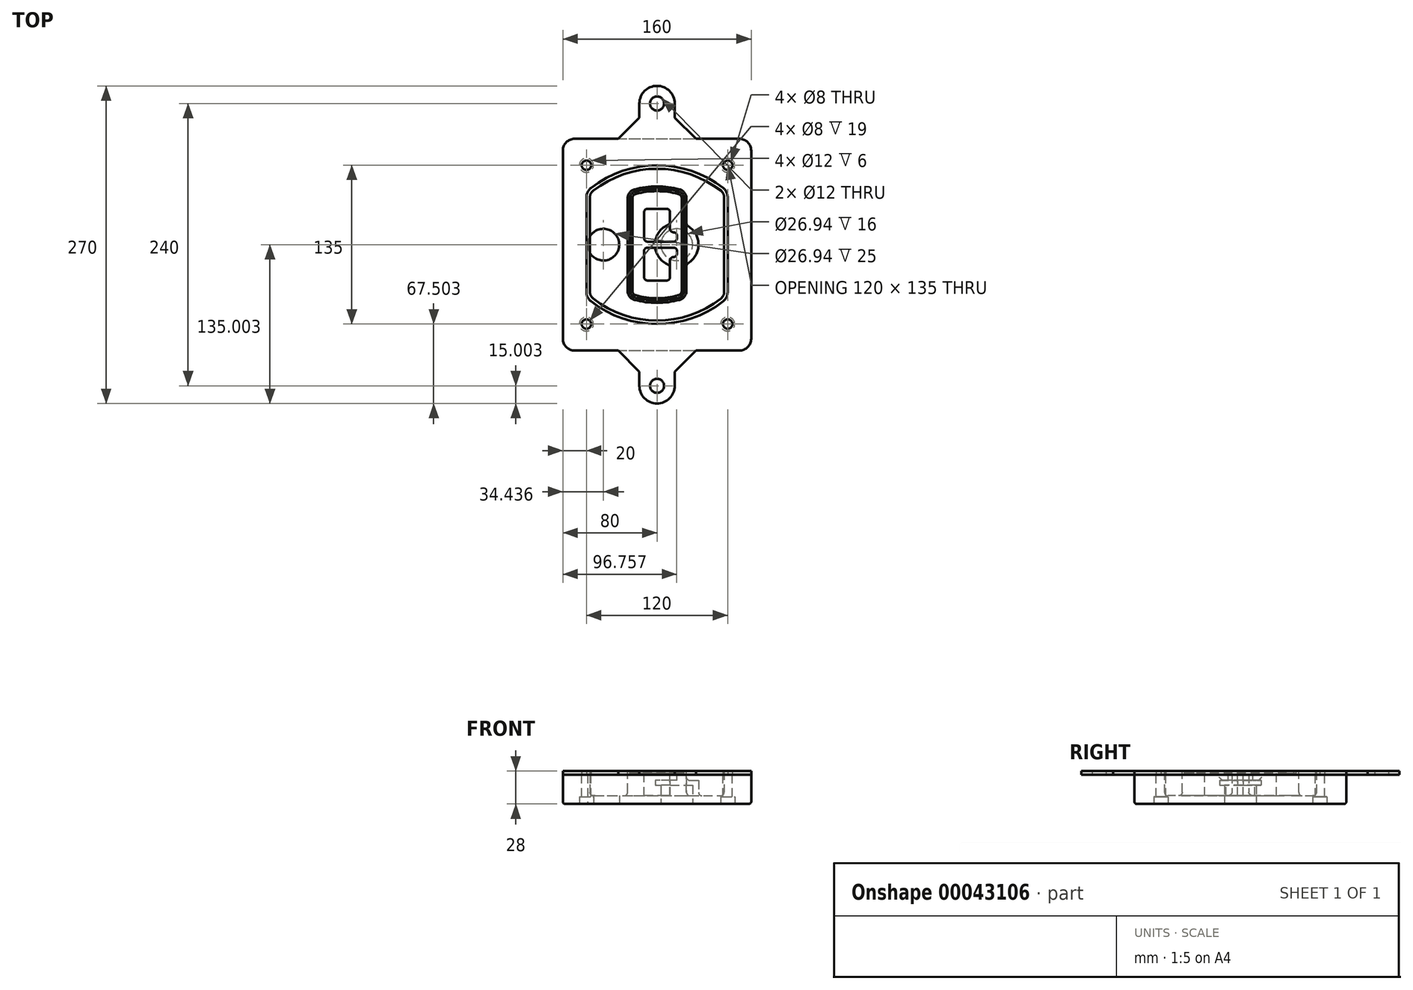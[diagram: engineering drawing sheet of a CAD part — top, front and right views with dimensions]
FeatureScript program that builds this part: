
annotation { "Feature Type Name" : "Feature", "Feature Type Description" : "" }
export const myFeature = defineFeature(function(context is Context, id is Id, definition is map)
    precondition{}
    {
        {
            var Q0;
            Q0=qCreatedBy(makeId("Top.planeOp"),FACE);
            var sketch = newSketch(context, id + "F0", { "sketchPlane" : qUnion([Q0])});
            skPoint(sketch, "E0.rect.middle", {"position": v(0, 0) * mm});
            skLineSegment(sketch, "E1.bottom", {"start": v(24.05, 28.38) * mm, "end": v(164.05, 28.38) * mm});
            skLineSegment(sketch, "E1.top", {"start": v(24.05, 208.38) * mm, "end": v(164.05, 208.38) * mm});
            skLineSegment(sketch, "E1.left", {"start": v(14.05, 38.38) * mm, "end": v(14.05, 198.38) * mm});
            skLineSegment(sketch, "E1.right", {"start": v(174.05, 38.38) * mm, "end": v(174.05, 198.38) * mm});
            skLineSegment(sketch, "E2", {"start": v(14.05, 208.38) * mm, "end": v(174.05, 28.38) * mm, "construction": true});
            skLineSegment(sketch, "E3", {"start": v(174.05, 208.38) * mm, "end": v(14.05, 28.38) * mm, "construction": true});
            skCircle(sketch, "E4", {"center": v(34.05, 185.88) * mm, "radius": 4 * mm});
            skCircle(sketch, "E5", {"center": v(154.05, 185.88) * mm, "radius": 4 * mm});
            skCircle(sketch, "E6", {"center": v(154.05, 50.88) * mm, "radius": 4 * mm});
            skCircle(sketch, "E7", {"center": v(34.05, 50.88) * mm, "radius": 4 * mm});
            skLineSegment(sketch, "E8", {"start": v(34.05, 185.88) * mm, "end": v(154.05, 185.88) * mm, "construction": true});
            skLineSegment(sketch, "E9", {"start": v(154.05, 185.88) * mm, "end": v(154.05, 50.88) * mm, "construction": true});
            skLineSegment(sketch, "E10", {"start": v(154.05, 50.88) * mm, "end": v(34.05, 50.88) * mm, "construction": true});
            skLineSegment(sketch, "E11", {"start": v(34.05, 50.88) * mm, "end": v(34.05, 185.88) * mm, "construction": true});
            skLineSegment(sketch, "E12", {"start": v(34.05, 158.68) * mm, "end": v(34.05, 78.09) * mm});
            skLineSegment(sketch, "E13", {"start": v(154.05, 158.68) * mm, "end": v(154.05, 78.09) * mm});
            skArc(sketch, "E14", {"start": v(150.2, 166.56) * mm, "mid": v(94.05, 185.88) * mm, "end": v(37.9, 166.56) * mm});
            skArc(sketch, "E15", {"start": v(37.9, 70.2) * mm, "mid": v(94.05, 50.88) * mm, "end": v(150.2, 70.2) * mm});
            skLineSegment(sketch, "E16", {"start": v(34.05, 118.38) * mm, "end": v(154.05, 118.38) * mm, "construction": true});
            skPoint(sketch, "E17.visualSharp", {"position": v(34.05, 73.38) * mm});
            skArc(sketch, "E17.filletArc", {"start": v(34.05, 78.09) * mm, "mid": v(35.06, 73.7) * mm, "end": v(37.9, 70.2) * mm});
            skPoint(sketch, "E18.visualSharp", {"position": v(34.05, 163.38) * mm});
            skArc(sketch, "E18.filletArc", {"start": v(37.9, 166.56) * mm, "mid": v(35.06, 163.06) * mm, "end": v(34.05, 158.68) * mm});
            skPoint(sketch, "E19.visualSharp", {"position": v(154.05, 163.38) * mm});
            skArc(sketch, "E19.filletArc", {"start": v(154.05, 158.68) * mm, "mid": v(153.04, 163.06) * mm, "end": v(150.2, 166.56) * mm});
            skPoint(sketch, "E20.visualSharp", {"position": v(154.05, 73.38) * mm});
            skArc(sketch, "E20.filletArc", {"start": v(150.2, 70.2) * mm, "mid": v(153.04, 73.7) * mm, "end": v(154.05, 78.09) * mm});
            skPoint(sketch, "E21.visualSharp", {"position": v(14.05, 208.38) * mm});
            skArc(sketch, "E21.filletArc", {"start": v(24.05, 208.38) * mm, "mid": v(16.98, 205.45) * mm, "end": v(14.05, 198.38) * mm});
            skPoint(sketch, "E22.visualSharp", {"position": v(174.05, 208.38) * mm});
            skArc(sketch, "E22.filletArc", {"start": v(174.05, 198.38) * mm, "mid": v(171.12, 205.45) * mm, "end": v(164.05, 208.38) * mm});
            skPoint(sketch, "E23.visualSharp", {"position": v(174.05, 28.38) * mm});
            skArc(sketch, "E23.filletArc", {"start": v(164.05, 28.38) * mm, "mid": v(171.12, 31.31) * mm, "end": v(174.05, 38.38) * mm});
            skPoint(sketch, "E24.visualSharp", {"position": v(14.05, 28.38) * mm});
            skArc(sketch, "E24.filletArc", {"start": v(14.05, 38.38) * mm, "mid": v(16.98, 31.31) * mm, "end": v(24.05, 28.38) * mm});
            skArc(sketch, "E25.0", {"start": v(151.05, 158.68) * mm, "mid": v(150.34, 161.75) * mm, "end": v(148.36, 164.2) * mm});
            skLineSegment(sketch, "E25.1", {"start": v(151.05, 158.68) * mm, "end": v(151.05, 78.09) * mm});
            skArc(sketch, "E25.2", {"start": v(148.36, 72.57) * mm, "mid": v(150.34, 75.02) * mm, "end": v(151.05, 78.09) * mm});
            skArc(sketch, "E25.3", {"start": v(39.74, 72.57) * mm, "mid": v(94.05, 53.88) * mm, "end": v(148.36, 72.57) * mm});
            skArc(sketch, "E25.4", {"start": v(37.05, 78.09) * mm, "mid": v(37.76, 75.02) * mm, "end": v(39.74, 72.57) * mm});
            skArc(sketch, "E25.5", {"start": v(148.36, 164.2) * mm, "mid": v(94.05, 182.88) * mm, "end": v(39.74, 164.2) * mm});
            skLineSegment(sketch, "E25.6", {"start": v(37.05, 158.68) * mm, "end": v(37.05, 78.09) * mm});
            skArc(sketch, "E25.7", {"start": v(39.74, 164.2) * mm, "mid": v(37.76, 161.75) * mm, "end": v(37.05, 158.68) * mm});
            skArc(sketch, "E26.0", {"start": v(35.43, 169.71) * mm, "mid": v(31.47, 164.82) * mm, "end": v(30.05, 158.68) * mm});
            skArc(sketch, "E26.1", {"start": v(152.67, 169.71) * mm, "mid": v(94.05, 189.88) * mm, "end": v(35.43, 169.71) * mm});
            skArc(sketch, "E26.2", {"start": v(158.05, 158.68) * mm, "mid": v(156.63, 164.82) * mm, "end": v(152.67, 169.71) * mm});
            skLineSegment(sketch, "E26.3", {"start": v(158.05, 158.68) * mm, "end": v(158.05, 78.09) * mm});
            skArc(sketch, "E26.4", {"start": v(152.67, 67.05) * mm, "mid": v(156.63, 71.95) * mm, "end": v(158.05, 78.09) * mm});
            skLineSegment(sketch, "E26.5", {"start": v(30.05, 158.68) * mm, "end": v(30.05, 78.09) * mm});
            skArc(sketch, "E26.6", {"start": v(35.43, 67.05) * mm, "mid": v(94.05, 46.88) * mm, "end": v(152.67, 67.05) * mm});
            skArc(sketch, "E26.7", {"start": v(30.05, 78.09) * mm, "mid": v(31.47, 71.95) * mm, "end": v(35.43, 67.05) * mm});
            skSolve(sketch);
        }
        {
            var Q0;
            Q0=makeQuery(id+"F0.imprint","IMPRINT",FACE,{"disambiguationData":[TD([[makeQuery(id+"F0.imprint","IMPRINT",EDGE,{"derivedFrom":sQuery(id+"F0.wireOp",EDGE,"E1.bottom")}),1.0]])]});
            var Q1;
            Q1=makeQuery(id+"F0.imprint","IMPRINT",FACE,{"disambiguationData":[TD([[makeQuery(id+"F0.imprint","IMPRINT",EDGE,{"derivedFrom":sQuery(id+"F0.wireOp",EDGE,"E12")}),1.0]])]});
            var Q2;
            Q2=makeQuery(id+"F0.imprint","IMPRINT",FACE,{"disambiguationData":[TD([[makeQuery(id+"F0.imprint","IMPRINT",EDGE,{"derivedFrom":sQuery(id+"F0.wireOp",EDGE,"E25.0")}),1.0]])]});
            var Q3;
            Q3=makeQuery(id+"F0.imprint","IMPRINT",FACE,{"disambiguationData":[TD([[makeQuery(id+"F0.imprint","IMPRINT",EDGE,{"derivedFrom":sQuery(id+"F0.wireOp",EDGE,"E12")}),-1.0]])]});
            extrude(context, id + "F1", {"entities" : qUnion([Q0, Q1, Q2, Q3]), "oppositeDirection" : true, "depth" : 25 * mm});
        }
        {
            var Q0;
            Q0=makeQuery(id+"F0.imprint","IMPRINT",FACE,{"disambiguationData":[TD([[makeQuery(id+"F0.imprint","IMPRINT",EDGE,{"derivedFrom":sQuery(id+"F0.wireOp",EDGE,"E12")}),1.0]])]});
            extrude(context, id + "F2", {"entities" : qUnion([Q0]), "operationType" : NewBodyOperationType.ADD, "depth" : 3 * mm});
        }
        {
            var Q0;
            Q0=makeQuery(id+"F0.imprint","IMPRINT",FACE,{"disambiguationData":[TD([[makeQuery(id+"F0.imprint","IMPRINT",EDGE,{"derivedFrom":sQuery(id+"F0.wireOp",EDGE,"E25.0")}),1.0]])]});
            extrude(context, id + "F3", {"entities" : qUnion([Q0]), "operationType" : NewBodyOperationType.REMOVE, "oppositeDirection" : true, "depth" : 18 * mm});
        }
        {
            var Q0;
            Q0=makeQuery(id+"F2.opExtrude","CAP_FACE",FACE,{"disambiguationData":[OSD([sQuery(id+"F0.wireOp",EDGE,"E12"),sQuery(id+"F0.wireOp",EDGE,"E13"),sQuery(id+"F0.wireOp",EDGE,"E14"),sQuery(id+"F0.wireOp",EDGE,"E15"),sQuery(id+"F0.wireOp",EDGE,"E17.filletArc"),sQuery(id+"F0.wireOp",EDGE,"E18.filletArc"),sQuery(id+"F0.wireOp",EDGE,"E19.filletArc"),sQuery(id+"F0.wireOp",EDGE,"E20.filletArc"),sQuery(id+"F0.wireOp",EDGE,"E25.0"),sQuery(id+"F0.wireOp",EDGE,"E25.1"),sQuery(id+"F0.wireOp",EDGE,"E25.2"),sQuery(id+"F0.wireOp",EDGE,"E25.3"),sQuery(id+"F0.wireOp",EDGE,"E25.4"),sQuery(id+"F0.wireOp",EDGE,"E25.5"),sQuery(id+"F0.wireOp",EDGE,"E25.6"),sQuery(id+"F0.wireOp",EDGE,"E25.7")])],"isStart":false});
            var sketch = newSketch(context, id + "F4", { "sketchPlane" : qUnion([Q0])});
            skArc(sketch, "E27.0", {"start": v(74.97, 71.41) * mm, "mid": v(94.05, 68.88) * mm, "end": v(113.13, 71.41) * mm});
            skArc(sketch, "E28.0", {"start": v(113.13, 165.35) * mm, "mid": v(94.05, 167.88) * mm, "end": v(74.97, 165.35) * mm});
            skLineSegment(sketch, "E29", {"start": v(69.05, 157.63) * mm, "end": v(69.05, 79.14) * mm});
            skLineSegment(sketch, "E30", {"start": v(119.05, 157.63) * mm, "end": v(119.05, 79.14) * mm});
            skLineSegment(sketch, "E31", {"start": v(69.05, 163.48) * mm, "end": v(119.05, 163.48) * mm, "construction": true});
            skLineSegment(sketch, "E32", {"start": v(69.05, 73.28) * mm, "end": v(119.05, 73.28) * mm, "construction": true});
            skPoint(sketch, "E33.visualSharp", {"position": v(69.05, 163.48) * mm});
            skArc(sketch, "E33.filletArc", {"start": v(74.97, 165.35) * mm, "mid": v(70.7, 162.5) * mm, "end": v(69.05, 157.63) * mm});
            skPoint(sketch, "E34.visualSharp", {"position": v(119.05, 163.48) * mm});
            skArc(sketch, "E34.filletArc", {"start": v(119.05, 157.63) * mm, "mid": v(117.4, 162.5) * mm, "end": v(113.13, 165.35) * mm});
            skPoint(sketch, "E35.visualSharp", {"position": v(119.05, 73.28) * mm});
            skArc(sketch, "E35.filletArc", {"start": v(113.13, 71.41) * mm, "mid": v(117.4, 74.27) * mm, "end": v(119.05, 79.14) * mm});
            skPoint(sketch, "E36.visualSharp", {"position": v(69.05, 73.28) * mm});
            skArc(sketch, "E36.filletArc", {"start": v(69.05, 79.14) * mm, "mid": v(70.7, 74.27) * mm, "end": v(74.97, 71.41) * mm});
            skArc(sketch, "E37.0", {"start": v(148.36, 164.2) * mm, "mid": v(94.05, 182.88) * mm, "end": v(39.74, 164.2) * mm});
            skArc(sketch, "E37.1", {"start": v(39.74, 164.2) * mm, "mid": v(37.76, 161.75) * mm, "end": v(37.05, 158.68) * mm});
            skLineSegment(sketch, "E37.2", {"start": v(37.05, 158.68) * mm, "end": v(37.05, 78.09) * mm});
            skArc(sketch, "E37.3", {"start": v(37.05, 78.09) * mm, "mid": v(37.76, 75.02) * mm, "end": v(39.74, 72.57) * mm});
            skArc(sketch, "E37.4", {"start": v(39.74, 72.57) * mm, "mid": v(94.05, 53.88) * mm, "end": v(148.36, 72.57) * mm});
            skArc(sketch, "E37.5", {"start": v(148.36, 72.57) * mm, "mid": v(150.34, 75.02) * mm, "end": v(151.05, 78.09) * mm});
            skLineSegment(sketch, "E37.6", {"start": v(151.05, 158.68) * mm, "end": v(151.05, 78.09) * mm});
            skArc(sketch, "E37.7", {"start": v(151.05, 158.68) * mm, "mid": v(150.34, 161.75) * mm, "end": v(148.36, 164.2) * mm});
            skLineSegment(sketch, "E38.0", {"start": v(117.05, 157.63) * mm, "end": v(117.05, 79.14) * mm});
            skArc(sketch, "E38.1", {"start": v(112.61, 73.34) * mm, "mid": v(115.81, 75.49) * mm, "end": v(117.05, 79.14) * mm});
            skArc(sketch, "E38.2", {"start": v(75.49, 73.34) * mm, "mid": v(94.05, 70.88) * mm, "end": v(112.61, 73.34) * mm});
            skArc(sketch, "E38.3", {"start": v(71.05, 79.14) * mm, "mid": v(72.29, 75.49) * mm, "end": v(75.49, 73.34) * mm});
            skLineSegment(sketch, "E38.4", {"start": v(71.05, 157.63) * mm, "end": v(71.05, 79.14) * mm});
            skArc(sketch, "E38.5", {"start": v(117.05, 157.63) * mm, "mid": v(115.81, 161.28) * mm, "end": v(112.61, 163.42) * mm});
            skArc(sketch, "E38.6", {"start": v(75.49, 163.42) * mm, "mid": v(72.29, 161.28) * mm, "end": v(71.05, 157.63) * mm});
            skArc(sketch, "E38.7", {"start": v(112.61, 163.42) * mm, "mid": v(94.05, 165.88) * mm, "end": v(75.49, 163.42) * mm});
            skArc(sketch, "E39.0", {"start": v(115.05, 157.63) * mm, "mid": v(114.23, 160.06) * mm, "end": v(112.1, 161.5) * mm});
            skLineSegment(sketch, "E39.1", {"start": v(115.05, 157.63) * mm, "end": v(115.05, 79.14) * mm});
            skArc(sketch, "E39.2", {"start": v(112.1, 75.27) * mm, "mid": v(114.23, 76.7) * mm, "end": v(115.05, 79.14) * mm});
            skArc(sketch, "E39.3", {"start": v(76, 75.27) * mm, "mid": v(94.05, 72.88) * mm, "end": v(112.1, 75.27) * mm});
            skArc(sketch, "E39.4", {"start": v(73.05, 79.14) * mm, "mid": v(73.87, 76.7) * mm, "end": v(76, 75.27) * mm});
            skArc(sketch, "E39.5", {"start": v(112.1, 161.5) * mm, "mid": v(94.05, 163.88) * mm, "end": v(76, 161.5) * mm});
            skLineSegment(sketch, "E39.6", {"start": v(73.05, 157.63) * mm, "end": v(73.05, 79.14) * mm});
            skArc(sketch, "E39.7", {"start": v(76, 161.5) * mm, "mid": v(73.87, 160.06) * mm, "end": v(73.05, 157.63) * mm});
            skLineSegment(sketch, "E40", {"start": v(69.05, 118.38) * mm, "end": v(119.05, 118.38) * mm, "construction": true});
            skLineSegment(sketch, "E41", {"start": v(83.05, 123.88) * mm, "end": v(83.05, 145.88) * mm});
            skLineSegment(sketch, "E42", {"start": v(86.05, 148.88) * mm, "end": v(102.05, 148.88) * mm});
            skLineSegment(sketch, "E43", {"start": v(105.05, 145.88) * mm, "end": v(105.05, 131.88) * mm});
            skLineSegment(sketch, "E44", {"start": v(108.05, 128.88) * mm, "end": v(108.05, 128.88) * mm});
            skLineSegment(sketch, "E45", {"start": v(111.05, 125.88) * mm, "end": v(111.05, 123.88) * mm});
            skLineSegment(sketch, "E46", {"start": v(108.05, 120.88) * mm, "end": v(86.05, 120.88) * mm});
            skPoint(sketch, "E47.visualSharp", {"position": v(83.05, 148.88) * mm});
            skArc(sketch, "E47.filletArc", {"start": v(86.05, 148.88) * mm, "mid": v(83.93, 148) * mm, "end": v(83.05, 145.88) * mm});
            skPoint(sketch, "E48.visualSharp", {"position": v(105.05, 148.88) * mm});
            skArc(sketch, "E48.filletArc", {"start": v(105.05, 145.88) * mm, "mid": v(104.17, 148) * mm, "end": v(102.05, 148.88) * mm});
            skPoint(sketch, "E49.visualSharp", {"position": v(105.05, 128.88) * mm});
            skArc(sketch, "E49.filletArc", {"start": v(105.05, 131.88) * mm, "mid": v(105.93, 129.76) * mm, "end": v(108.05, 128.88) * mm});
            skPoint(sketch, "E50.visualSharp", {"position": v(111.05, 128.88) * mm});
            skArc(sketch, "E50.filletArc", {"start": v(111.05, 125.88) * mm, "mid": v(110.17, 128) * mm, "end": v(108.05, 128.88) * mm});
            skPoint(sketch, "E51.visualSharp", {"position": v(111.05, 120.88) * mm});
            skArc(sketch, "E51.filletArc", {"start": v(108.05, 120.88) * mm, "mid": v(110.17, 121.76) * mm, "end": v(111.05, 123.88) * mm});
            skPoint(sketch, "E52.visualSharp", {"position": v(83.05, 120.88) * mm});
            skArc(sketch, "E52.filletArc", {"start": v(83.05, 123.88) * mm, "mid": v(83.93, 121.76) * mm, "end": v(86.05, 120.88) * mm});
            skLineSegment(sketch, "E53.0.MirrorCS", {"start": v(108.05, 115.88) * mm, "end": v(86.05, 115.88) * mm});
            skArc(sketch, "E54.0.MirrorCS", {"start": v(83.05, 112.88) * mm, "mid": v(83.93, 115) * mm, "end": v(86.05, 115.88) * mm});
            skLineSegment(sketch, "E55.0.MirrorCS", {"start": v(83.05, 112.88) * mm, "end": v(83.05, 90.88) * mm});
            skArc(sketch, "E56.0.MirrorCS", {"start": v(86.05, 87.88) * mm, "mid": v(83.93, 88.76) * mm, "end": v(83.05, 90.88) * mm});
            skLineSegment(sketch, "E57.0.MirrorCS", {"start": v(86.05, 87.88) * mm, "end": v(102.05, 87.88) * mm});
            skArc(sketch, "E58.0.MirrorCS", {"start": v(105.05, 90.88) * mm, "mid": v(104.17, 88.76) * mm, "end": v(102.05, 87.88) * mm});
            skLineSegment(sketch, "E59.0.MirrorCS", {"start": v(105.05, 90.88) * mm, "end": v(105.05, 104.88) * mm});
            skArc(sketch, "E60.0.MirrorCS", {"start": v(105.05, 104.88) * mm, "mid": v(105.93, 107) * mm, "end": v(108.05, 107.88) * mm});
            skArc(sketch, "E61.0.MirrorCS", {"start": v(111.05, 110.88) * mm, "mid": v(110.17, 108.76) * mm, "end": v(108.05, 107.88) * mm});
            skLineSegment(sketch, "E62.0.MirrorCS", {"start": v(111.05, 110.88) * mm, "end": v(111.05, 112.88) * mm});
            skArc(sketch, "E63.0.MirrorCS", {"start": v(108.05, 115.88) * mm, "mid": v(110.17, 115) * mm, "end": v(111.05, 112.88) * mm});
            skSolve(sketch);
        }
        {
            var Q0;
            Q0=makeQuery(id+"F4.imprint","IMPRINT",FACE,{"disambiguationData":[TD([[makeQuery(id+"F4.imprint","IMPRINT",EDGE,{"derivedFrom":sQuery(id+"F4.wireOp",EDGE,"E27.0")}),1.0]])]});
            var Q1;
            Q1=makeQuery(id+"F4.imprint","IMPRINT",FACE,{"disambiguationData":[TD([[makeQuery(id+"F4.imprint","IMPRINT",EDGE,{"derivedFrom":sQuery(id+"F4.wireOp",EDGE,"E38.0")}),-1.0]])]});
            var Q2;
            Q2=makeQuery(id+"F4.imprint","IMPRINT",FACE,{"disambiguationData":[TD([[makeQuery(id+"F4.imprint","IMPRINT",EDGE,{"derivedFrom":sQuery(id+"F4.wireOp",EDGE,"E39.0")}),1.0]])]});
            extrude(context, id + "F5", {"entities" : qUnion([Q0, Q1, Q2]), "operationType" : NewBodyOperationType.ADD, "endBound" : BoundingType.UP_TO_NEXT, "oppositeDirection" : true, "depth" : 25 * mm});
        }
        {
            var Q0;
            Q0=makeQuery(id+"F4.imprint","IMPRINT",FACE,{"disambiguationData":[TD([[makeQuery(id+"F4.imprint","IMPRINT",EDGE,{"derivedFrom":sQuery(id+"F4.wireOp",EDGE,"E38.0")}),-1.0]])]});
            extrude(context, id + "F6", {"entities" : qUnion([Q0]), "operationType" : NewBodyOperationType.REMOVE, "oppositeDirection" : true, "depth" : 2 * mm});
        }
        {
            var Q0;
            Q0=makeQuery(id+"F1.opExtrude","CAP_FACE",FACE,{"disambiguationData":[OSD([sQuery(id+"F0.wireOp",EDGE,"E1.bottom"),sQuery(id+"F0.wireOp",EDGE,"E1.top"),sQuery(id+"F0.wireOp",EDGE,"E1.left"),sQuery(id+"F0.wireOp",EDGE,"E1.right"),sQuery(id+"F0.wireOp",EDGE,"E4"),sQuery(id+"F0.wireOp",EDGE,"E5"),sQuery(id+"F0.wireOp",EDGE,"E6"),sQuery(id+"F0.wireOp",EDGE,"E7"),sQuery(id+"F0.wireOp",EDGE,"E21.filletArc"),sQuery(id+"F0.wireOp",EDGE,"E22.filletArc"),sQuery(id+"F0.wireOp",EDGE,"E23.filletArc"),sQuery(id+"F0.wireOp",EDGE,"E24.filletArc")])],"isStart":false});
            var sketch = newSketch(context, id + "F7", { "sketchPlane" : qUnion([Q0])});
            skCircle(sketch, "E64", {"center": v(110.8, -118.38) * mm, "radius": 13.47 * mm});
            skCircle(sketch, "E65", {"center": v(48.49, -118.38) * mm, "radius": 13.47 * mm});
            skLineSegment(sketch, "E66", {"start": v(174.05, -118.38) * mm, "end": v(14.05, -118.38) * mm});
            skCircle(sketch, "E67", {"center": v(110.8, -118.38) * mm, "radius": 18.47 * mm});
            skCircle(sketch, "E68", {"center": v(154.05, -185.88) * mm, "radius": 6 * mm});
            skCircle(sketch, "E69", {"center": v(34.05, -185.88) * mm, "radius": 6 * mm});
            skCircle(sketch, "E70", {"center": v(34.05, -50.88) * mm, "radius": 6 * mm});
            skCircle(sketch, "E71", {"center": v(154.05, -50.88) * mm, "radius": 6 * mm});
            skSolve(sketch);
        }
        {
            var Q0;
            {var subQ1=sQuery(id+"F7.wireOp",EDGE,"E66");var subQ4=sQuery(id+"F7.wireOp",EDGE,"E64");var subQ6=makeQuery(id+"F7.imprint","INTERSECT",VERTEX,{"disambiguationData":[OD(0.0)],"derivedFrom":[subQ4,subQ1]});Q0=makeQuery(id+"F7.imprint","IMPRINT",FACE,{"disambiguationData":[TD([[makeQuery(id+"F7.imprint","IMPRINT",EDGE,{"disambiguationData":[TD([[subQ6,-1.0]])],"derivedFrom":subQ4}),-1.0]])]});}
            var Q1;
            {var subQ0=sQuery(id+"F7.wireOp",EDGE,"E66");var subQ1=sQuery(id+"F7.wireOp",EDGE,"E64");var subQ3=makeQuery(id+"F7.imprint","INTERSECT",VERTEX,{"disambiguationData":[OD(0.0)],"derivedFrom":[subQ1,subQ0]});Q1=makeQuery(id+"F7.imprint","IMPRINT",FACE,{"disambiguationData":[TD([[makeQuery(id+"F7.imprint","IMPRINT",EDGE,{"disambiguationData":[TD([[subQ3,-1.0]])],"derivedFrom":subQ1}),1.0]])]});}
            var Q2;
            {var subQ0=sQuery(id+"F7.wireOp",EDGE,"E66");var subQ1=sQuery(id+"F7.wireOp",EDGE,"E64");var subQ3=makeQuery(id+"F7.imprint","INTERSECT",VERTEX,{"disambiguationData":[OD(0.0)],"derivedFrom":[subQ1,subQ0]});Q2=makeQuery(id+"F7.imprint","IMPRINT",FACE,{"disambiguationData":[TD([[makeQuery(id+"F7.imprint","IMPRINT",EDGE,{"disambiguationData":[TD([[subQ3,1.0]])],"derivedFrom":subQ1}),1.0]])]});}
            var Q3;
            {var subQ1=sQuery(id+"F7.wireOp",EDGE,"E66");var subQ4=sQuery(id+"F7.wireOp",EDGE,"E64");var subQ6=makeQuery(id+"F7.imprint","INTERSECT",VERTEX,{"disambiguationData":[OD(0.0)],"derivedFrom":[subQ4,subQ1]});Q3=makeQuery(id+"F7.imprint","IMPRINT",FACE,{"disambiguationData":[TD([[makeQuery(id+"F7.imprint","IMPRINT",EDGE,{"disambiguationData":[TD([[subQ6,1.0]])],"derivedFrom":subQ4}),-1.0]])]});}
            extrude(context, id + "F8", {"entities" : qUnion([Q0, Q1, Q2, Q3]), "operationType" : NewBodyOperationType.ADD, "oppositeDirection" : true, "depth" : 20 * mm});
        }
        {
            var Q0;
            {var subQ0=sQuery(id+"F7.wireOp",EDGE,"E66");var subQ1=sQuery(id+"F7.wireOp",EDGE,"E64");var subQ3=makeQuery(id+"F7.imprint","INTERSECT",VERTEX,{"disambiguationData":[OD(0.0)],"derivedFrom":[subQ1,subQ0]});Q0=makeQuery(id+"F7.imprint","IMPRINT",FACE,{"disambiguationData":[TD([[makeQuery(id+"F7.imprint","IMPRINT",EDGE,{"disambiguationData":[TD([[subQ3,-1.0]])],"derivedFrom":subQ1}),1.0]])]});}
            var Q1;
            {var subQ0=sQuery(id+"F7.wireOp",EDGE,"E66");var subQ1=sQuery(id+"F7.wireOp",EDGE,"E64");var subQ3=makeQuery(id+"F7.imprint","INTERSECT",VERTEX,{"disambiguationData":[OD(0.0)],"derivedFrom":[subQ1,subQ0]});Q1=makeQuery(id+"F7.imprint","IMPRINT",FACE,{"disambiguationData":[TD([[makeQuery(id+"F7.imprint","IMPRINT",EDGE,{"disambiguationData":[TD([[subQ3,1.0]])],"derivedFrom":subQ1}),1.0]])]});}
            extrude(context, id + "F9", {"entities" : qUnion([Q0, Q1]), "operationType" : NewBodyOperationType.REMOVE, "oppositeDirection" : true, "depth" : 16 * mm});
        }
        {
            var Q0;
            {var subQ0=sQuery(id+"F7.wireOp",EDGE,"E66");var subQ1=sQuery(id+"F7.wireOp",EDGE,"E65");var subQ3=makeQuery(id+"F7.imprint","INTERSECT",VERTEX,{"disambiguationData":[OD(0.0)],"derivedFrom":[subQ1,subQ0]});Q0=makeQuery(id+"F7.imprint","IMPRINT",FACE,{"disambiguationData":[TD([[makeQuery(id+"F7.imprint","IMPRINT",EDGE,{"disambiguationData":[TD([[subQ3,-1.0]])],"derivedFrom":subQ1}),1.0]])]});}
            var Q1;
            {var subQ0=sQuery(id+"F7.wireOp",EDGE,"E66");var subQ1=sQuery(id+"F7.wireOp",EDGE,"E65");var subQ3=makeQuery(id+"F7.imprint","INTERSECT",VERTEX,{"disambiguationData":[OD(0.0)],"derivedFrom":[subQ1,subQ0]});Q1=makeQuery(id+"F7.imprint","IMPRINT",FACE,{"disambiguationData":[TD([[makeQuery(id+"F7.imprint","IMPRINT",EDGE,{"disambiguationData":[TD([[subQ3,1.0]])],"derivedFrom":subQ1}),1.0]])]});}
            extrude(context, id + "F10", {"entities" : qUnion([Q0, Q1]), "operationType" : NewBodyOperationType.REMOVE, "oppositeDirection" : true, "depth" : 25 * mm});
        }
        {
            var Q0;
            Q0=makeQuery(id+"F7.imprint","IMPRINT",FACE,{"disambiguationData":[TD([[makeQuery(id+"F7.imprint","IMPRINT",EDGE,{"derivedFrom":sQuery(id+"F7.wireOp",EDGE,"E68")}),1.0]])]});
            var Q1;
            Q1=makeQuery(id+"F7.imprint","IMPRINT",FACE,{"disambiguationData":[TD([[makeQuery(id+"F7.imprint","IMPRINT",EDGE,{"derivedFrom":makeQuery(id+"F1.opExtrude","CAP_EDGE",EDGE,{"disambiguationData":[OSD([sQuery(id+"F0.wireOp",EDGE,"E5")])],"isStart":false})}),-1.0]])]});
            var Q2;
            Q2=makeQuery(id+"F7.imprint","IMPRINT",FACE,{"disambiguationData":[TD([[makeQuery(id+"F7.imprint","IMPRINT",EDGE,{"derivedFrom":sQuery(id+"F7.wireOp",EDGE,"E69")}),1.0]])]});
            var Q3;
            Q3=makeQuery(id+"F7.imprint","IMPRINT",FACE,{"disambiguationData":[TD([[makeQuery(id+"F7.imprint","IMPRINT",EDGE,{"derivedFrom":makeQuery(id+"F1.opExtrude","CAP_EDGE",EDGE,{"disambiguationData":[OSD([sQuery(id+"F0.wireOp",EDGE,"E4")])],"isStart":false})}),-1.0]])]});
            var Q4;
            Q4=makeQuery(id+"F7.imprint","IMPRINT",FACE,{"disambiguationData":[TD([[makeQuery(id+"F7.imprint","IMPRINT",EDGE,{"derivedFrom":sQuery(id+"F7.wireOp",EDGE,"E70")}),1.0]])]});
            var Q5;
            Q5=makeQuery(id+"F7.imprint","IMPRINT",FACE,{"disambiguationData":[TD([[makeQuery(id+"F7.imprint","IMPRINT",EDGE,{"derivedFrom":makeQuery(id+"F1.opExtrude","CAP_EDGE",EDGE,{"disambiguationData":[OSD([sQuery(id+"F0.wireOp",EDGE,"E7")])],"isStart":false})}),-1.0]])]});
            var Q6;
            Q6=makeQuery(id+"F7.imprint","IMPRINT",FACE,{"disambiguationData":[TD([[makeQuery(id+"F7.imprint","IMPRINT",EDGE,{"derivedFrom":sQuery(id+"F7.wireOp",EDGE,"E71")}),1.0]])]});
            var Q7;
            Q7=makeQuery(id+"F7.imprint","IMPRINT",FACE,{"disambiguationData":[TD([[makeQuery(id+"F7.imprint","IMPRINT",EDGE,{"derivedFrom":makeQuery(id+"F1.opExtrude","CAP_EDGE",EDGE,{"disambiguationData":[OSD([sQuery(id+"F0.wireOp",EDGE,"E6")])],"isStart":false})}),-1.0]])]});
            extrude(context, id + "F11", {"entities" : qUnion([Q0, Q1, Q2, Q3, Q4, Q5, Q6, Q7]), "operationType" : NewBodyOperationType.REMOVE, "oppositeDirection" : true, "depth" : 6 * mm});
        }
        {
            var Q0;
            Q0=makeQuery(id+"F9.boolean.opBoolean","COPY",FACE,{"derivedFrom":makeQuery(id+"F9.opExtrude","CAP_FACE",FACE,{"disambiguationData":[OSD([sQuery(id+"F7.wireOp",EDGE,"E64")])],"isStart":false})});
            var sketch = newSketch(context, id + "F12", { "sketchPlane" : qUnion([Q0])});
            skArc(sketch, "E72.0", {"start": v(105.05, -100.83) * mm, "mid": v(96.62, -106.56) * mm, "end": v(92.5, -115.88) * mm});
            skArc(sketch, "E72.1", {"start": v(92.5, -120.88) * mm, "mid": v(96.62, -130.2) * mm, "end": v(105.05, -135.93) * mm});
            skLineSegment(sketch, "E73", {"start": v(92.5, -120.88) * mm, "end": v(108.05, -120.88) * mm});
            skLineSegment(sketch, "E74.0", {"start": v(108.05, -115.88) * mm, "end": v(92.5, -115.88) * mm});
            skArc(sketch, "E74.1", {"start": v(108.05, -115.88) * mm, "mid": v(110.17, -115) * mm, "end": v(111.05, -112.88) * mm});
            skLineSegment(sketch, "E74.2", {"start": v(111.05, -110.88) * mm, "end": v(111.05, -112.88) * mm});
            skArc(sketch, "E74.3", {"start": v(111.05, -110.88) * mm, "mid": v(110.17, -108.76) * mm, "end": v(108.05, -107.88) * mm});
            skArc(sketch, "E74.4", {"start": v(105.05, -104.88) * mm, "mid": v(105.93, -107) * mm, "end": v(108.05, -107.88) * mm});
            skLineSegment(sketch, "E74.5", {"start": v(105.05, -100.83) * mm, "end": v(105.05, -104.88) * mm});
            skLineSegment(sketch, "E74.7", {"start": v(108.05, -120.88) * mm, "end": v(92.5, -120.88) * mm});
            skArc(sketch, "E74.8", {"start": v(108.05, -120.88) * mm, "mid": v(110.17, -121.76) * mm, "end": v(111.05, -123.88) * mm});
            skLineSegment(sketch, "E74.9", {"start": v(111.05, -125.88) * mm, "end": v(111.05, -123.88) * mm});
            skArc(sketch, "E74.10", {"start": v(111.05, -125.88) * mm, "mid": v(110.17, -128) * mm, "end": v(108.05, -128.88) * mm});
            skArc(sketch, "E74.11", {"start": v(105.05, -131.88) * mm, "mid": v(105.93, -129.76) * mm, "end": v(108.05, -128.88) * mm});
            skLineSegment(sketch, "E74.12", {"start": v(105.05, -135.93) * mm, "end": v(105.05, -131.88) * mm});
            skPoint(sketch, "E75.orphan", {"position": v(105.05, -145.88) * mm});
            skPoint(sketch, "E76.orphan", {"position": v(86.05, -120.88) * mm});
            skPoint(sketch, "E77.orphan", {"position": v(86.05, -115.88) * mm});
            skPoint(sketch, "E78.orphan", {"position": v(105.05, -90.88) * mm});
            skSolve(sketch);
        }
        {
            var Q0;
            {var subQ7=sQuery(id+"F12.wireOp",EDGE,"E72.0");var subQ14=sQuery(id+"F12.wireOp",EDGE,"E72.1");var subQ16=sQuery(id+"F12.wireOp",EDGE,"E74.1");var subQ18=sQuery(id+"F12.wireOp",EDGE,"E74.8");Q0=qUnion([makeQuery(id+"F12.imprint","IMPRINT",FACE,{"disambiguationData":[TD([[makeQuery(id+"F12.imprint","IMPRINT",EDGE,{"derivedFrom":subQ7}),1.0]])]}),makeQuery(id+"F12.imprint","IMPRINT",FACE,{"disambiguationData":[TD([[makeQuery(id+"F12.imprint","IMPRINT",EDGE,{"derivedFrom":subQ14}),1.0]])]}),makeQuery(id+"F12.imprint","IMPRINT",FACE,{"disambiguationData":[TD([[makeQuery(id+"F12.imprint","IMPRINT",EDGE,{"derivedFrom":subQ16}),1.0]])]}),makeQuery(id+"F12.imprint","IMPRINT",FACE,{"disambiguationData":[TD([[makeQuery(id+"F12.imprint","IMPRINT",EDGE,{"derivedFrom":subQ18}),-1.0]])]})]);}
            var Q1;
            Q1=makeQuery(id+"F5.boolean.opBoolean","SPLIT",FACE,{"disambiguationData":[TD([makeQuery(id+"F5.opExtrude","SWEPT_FACE",FACE,{"disambiguationData":[OSD([sQuery(id+"F4.wireOp",EDGE,"E41")])]})])],"derivedFrom":makeQuery(id+"F3.boolean.opBoolean","COPY",FACE,{"derivedFrom":makeQuery(id+"F3.opExtrude","CAP_FACE",FACE,{"disambiguationData":[OSD([sQuery(id+"F0.wireOp",EDGE,"E25.0"),sQuery(id+"F0.wireOp",EDGE,"E25.1"),sQuery(id+"F0.wireOp",EDGE,"E25.2"),sQuery(id+"F0.wireOp",EDGE,"E25.3"),sQuery(id+"F0.wireOp",EDGE,"E25.4"),sQuery(id+"F0.wireOp",EDGE,"E25.5"),sQuery(id+"F0.wireOp",EDGE,"E25.6"),sQuery(id+"F0.wireOp",EDGE,"E25.7")])],"isStart":false})})});
            extrude(context, id + "F13", {"entities" : qUnion([Q0]), "operationType" : NewBodyOperationType.REMOVE, "endBound" : BoundingType.UP_TO_SURFACE, "endBoundEntityFace" : qUnion([Q1]), "depth" : 25 * mm});
        }
        {
            var Q0;
            Q0=makeQuery(id+"F3.boolean.opBoolean","COPY",EDGE,{"derivedFrom":makeQuery(id+"F3.opExtrude","CAP_EDGE",EDGE,{"disambiguationData":[OSD([sQuery(id+"F0.wireOp",EDGE,"E25.6")])],"isStart":false})});
            var Q1;
            Q1=makeQuery(id+"F8.boolean.opBoolean","INTERSECT",EDGE,{"derivedFrom":[makeQuery(id+"F5.opExtrude","SWEPT_FACE",FACE,{"disambiguationData":[OSD([sQuery(id+"F4.wireOp",EDGE,"E30")])]}),makeQuery(id+"F8.opExtrude","CAP_FACE",FACE,{"disambiguationData":[OSD([sQuery(id+"F7.wireOp",EDGE,"E67")])],"isStart":false})]});
            var Q2;
            Q2=makeQuery(id+"F8.boolean.opBoolean","INTERSECT",EDGE,{"disambiguationData":[OD(1.0)],"derivedFrom":[makeQuery(id+"F5.opExtrude","SWEPT_FACE",FACE,{"disambiguationData":[OSD([sQuery(id+"F4.wireOp",EDGE,"E30")])]}),makeQuery(id+"F8.opExtrude","SWEPT_FACE",FACE,{"disambiguationData":[OSD([sQuery(id+"F7.wireOp",EDGE,"E67")])]})]});
            var Q3;
            {var subQ0=sQuery(id+"F4.wireOp",EDGE,"E30");Q3=makeQuery(id+"F8.boolean.opBoolean","SPLIT",EDGE,{"disambiguationData":[TD([makeQuery(id+"F5.opExtrude","SWEPT_FACE",FACE,{"disambiguationData":[OSD([sQuery(id+"F4.wireOp",EDGE,"E35.filletArc")])]})])],"derivedFrom":makeQuery(id+"F5.opExtrude","CAP_EDGE",EDGE,{"disambiguationData":[OSD([subQ0])],"isStart":false})});}
            var Q4;
            {var subQ0=sQuery(id+"F0.wireOp",EDGE,"E25.7");var subQ1=sQuery(id+"F0.wireOp",EDGE,"E25.1");var subQ2=sQuery(id+"F0.wireOp",EDGE,"E25.6");var subQ3=sQuery(id+"F0.wireOp",EDGE,"E25.5");var subQ4=sQuery(id+"F0.wireOp",EDGE,"E25.4");var subQ5=sQuery(id+"F0.wireOp",EDGE,"E25.0");var subQ6=sQuery(id+"F0.wireOp",EDGE,"E25.2");var subQ7=sQuery(id+"F0.wireOp",EDGE,"E25.3");Q4=makeQuery(id+"F8.boolean.opBoolean","INTERSECT",EDGE,{"derivedFrom":[makeQuery(id+"F5.boolean.opBoolean","SPLIT",FACE,{"disambiguationData":[TD([makeQuery(id+"F2.opExtrude","SWEPT_FACE",FACE,{"disambiguationData":[OSD([subQ5])]})])],"derivedFrom":makeQuery(id+"F3.boolean.opBoolean","COPY",FACE,{"derivedFrom":makeQuery(id+"F3.opExtrude","CAP_FACE",FACE,{"disambiguationData":[OSD([subQ5,subQ1,subQ6,subQ7,subQ4,subQ3,subQ2,subQ0])],"isStart":false})})}),makeQuery(id+"F8.opExtrude","SWEPT_FACE",FACE,{"disambiguationData":[OSD([sQuery(id+"F7.wireOp",EDGE,"E67")])]})]});}
            var Q5;
            Q5=makeQuery(id+"F8.boolean.opBoolean","INTERSECT",EDGE,{"disambiguationData":[OD(0.0)],"derivedFrom":[makeQuery(id+"F5.opExtrude","SWEPT_FACE",FACE,{"disambiguationData":[OSD([sQuery(id+"F4.wireOp",EDGE,"E30")])]}),makeQuery(id+"F8.opExtrude","SWEPT_FACE",FACE,{"disambiguationData":[OSD([sQuery(id+"F7.wireOp",EDGE,"E67")])]})]});
            fillet(context, id + "F14", {"entities" : qUnion([Q0, Q1, Q2, Q3, Q4, Q5]), "radius" : 3 * mm, "tangentPropagation" : true, "allowEdgeOverflow" : false});
        }
        {
            var Q0;
            Q0=makeQuery(id+"F1.opExtrude","CAP_EDGE",EDGE,{"disambiguationData":[OSD([sQuery(id+"F0.wireOp",EDGE,"E1.bottom")])],"isStart":false});
            fillet(context, id + "F15", {"entities" : qUnion([Q0]), "radius" : 2 * mm, "tangentPropagation" : true, "allowEdgeOverflow" : false});
        }
        {
            var Q0;
            {var subQ0=sQuery(id+"F0.wireOp",EDGE,"E1.bottom");var subQ1=sQuery(id+"F0.wireOp",EDGE,"E1.top");var subQ2=sQuery(id+"F0.wireOp",EDGE,"E1.left");var subQ3=sQuery(id+"F0.wireOp",EDGE,"E1.right");var subQ4=sQuery(id+"F0.wireOp",EDGE,"E4");var subQ5=sQuery(id+"F0.wireOp",EDGE,"E5");var subQ6=sQuery(id+"F0.wireOp",EDGE,"E6");var subQ7=sQuery(id+"F0.wireOp",EDGE,"E7");var subQ8=sQuery(id+"F0.wireOp",EDGE,"E21.filletArc");var subQ9=sQuery(id+"F0.wireOp",EDGE,"E22.filletArc");var subQ10=sQuery(id+"F0.wireOp",EDGE,"E23.filletArc");var subQ11=sQuery(id+"F0.wireOp",EDGE,"E24.filletArc");Q0=makeQuery(id+"F2.boolean.opBoolean","SPLIT",FACE,{"disambiguationData":[TD([makeQuery(id+"F1.opExtrude","SWEPT_FACE",FACE,{"disambiguationData":[OSD([subQ0])]})])],"derivedFrom":makeQuery(id+"F1.opExtrude","CAP_FACE",FACE,{"disambiguationData":[OSD([subQ0,subQ1,subQ2,subQ3,subQ4,subQ5,subQ6,subQ7,subQ8,subQ9,subQ10,subQ11])],"isStart":true})});}
            var sketch = newSketch(context, id + "F16", { "sketchPlane" : qUnion([Q0])});
            skLineSegment(sketch, "E79", {"start": v(94.05, 208.38) * mm, "end": v(94.05, 238.38) * mm, "construction": true});
            skCircle(sketch, "E80", {"center": v(94.05, 238.38) * mm, "radius": 6 * mm});
            skLineSegment(sketch, "E81", {"start": v(127.05, 208.38) * mm, "end": v(109.05, 226.38) * mm});
            skLineSegment(sketch, "E82", {"start": v(109.05, 226.38) * mm, "end": v(109.05, 238.38) * mm});
            skLineSegment(sketch, "E83", {"start": v(61.05, 208.38) * mm, "end": v(79.05, 226.38) * mm});
            skLineSegment(sketch, "E84", {"start": v(79.05, 226.38) * mm, "end": v(79.05, 238.38) * mm});
            skArc(sketch, "E85", {"start": v(109.05, 238.38) * mm, "mid": v(94.05, 253.38) * mm, "end": v(79.05, 238.38) * mm});
            skLineSegment(sketch, "E86", {"start": v(174.05, 118.38) * mm, "end": v(14.05, 118.38) * mm, "construction": true});
            skLineSegment(sketch, "E87.MirrorCS", {"start": v(94.05, 28.38) * mm, "end": v(94.05, -1.62) * mm});
            skLineSegment(sketch, "E88.MirrorCS", {"start": v(127.05, 28.38) * mm, "end": v(109.05, 10.38) * mm});
            skLineSegment(sketch, "E89.MirrorCS", {"start": v(109.05, 10.38) * mm, "end": v(109.05, -1.62) * mm});
            skArc(sketch, "E90.MirrorCS", {"start": v(109.05, -1.62) * mm, "mid": v(94.05, -16.62) * mm, "end": v(79.05, -1.62) * mm});
            skLineSegment(sketch, "E91.MirrorCS", {"start": v(79.05, 10.38) * mm, "end": v(79.05, -1.62) * mm});
            skLineSegment(sketch, "E92.MirrorCS", {"start": v(61.05, 28.38) * mm, "end": v(79.05, 10.38) * mm});
            skCircle(sketch, "E93.MirrorC", {"center": v(94.05, -1.62) * mm, "radius": 6 * mm});
            skSolve(sketch);
        }
        {
            var Q0;
            Q0=makeQuery(id+"F16.imprint","IMPRINT",FACE,{"disambiguationData":[TD([[makeQuery(id+"F16.imprint","IMPRINT",EDGE,{"derivedFrom":sQuery(id+"F16.wireOp",EDGE,"E89.MirrorCS")}),-1.0]])]});
            var Q1;
            Q1=makeQuery(id+"F16.imprint","IMPRINT",FACE,{"disambiguationData":[TD([[makeQuery(id+"F16.imprint","IMPRINT",EDGE,{"derivedFrom":sQuery(id+"F16.wireOp",EDGE,"E80")}),-1.0]])]});
            var Q2;
            Q2=makeQuery(id+"F16.imprint","IMPRINT",FACE,{"disambiguationData":[TD([[makeQuery(id+"F16.imprint","IMPRINT",EDGE,{"derivedFrom":makeQuery(id+"F1.opExtrude","CAP_EDGE",EDGE,{"disambiguationData":[OSD([sQuery(id+"F0.wireOp",EDGE,"E1.left")])],"isStart":true})}),-1.0]])]});
            var Q3;
            Q3=makeQuery(id+"F2.opExtrude","CAP_FACE",FACE,{"disambiguationData":[OSD([sQuery(id+"F0.wireOp",EDGE,"E12"),sQuery(id+"F0.wireOp",EDGE,"E13"),sQuery(id+"F0.wireOp",EDGE,"E14"),sQuery(id+"F0.wireOp",EDGE,"E15"),sQuery(id+"F0.wireOp",EDGE,"E17.filletArc"),sQuery(id+"F0.wireOp",EDGE,"E18.filletArc"),sQuery(id+"F0.wireOp",EDGE,"E19.filletArc"),sQuery(id+"F0.wireOp",EDGE,"E20.filletArc"),sQuery(id+"F0.wireOp",EDGE,"E25.0"),sQuery(id+"F0.wireOp",EDGE,"E25.1"),sQuery(id+"F0.wireOp",EDGE,"E25.2"),sQuery(id+"F0.wireOp",EDGE,"E25.3"),sQuery(id+"F0.wireOp",EDGE,"E25.4"),sQuery(id+"F0.wireOp",EDGE,"E25.5"),sQuery(id+"F0.wireOp",EDGE,"E25.6"),sQuery(id+"F0.wireOp",EDGE,"E25.7")])],"isStart":false});
            extrude(context, id + "F17", {"entities" : qUnion([Q0, Q1, Q2]), "endBound" : BoundingType.UP_TO_SURFACE, "endBoundEntityFace" : qUnion([Q3]), "depth" : 25 * mm});
        }
    });
